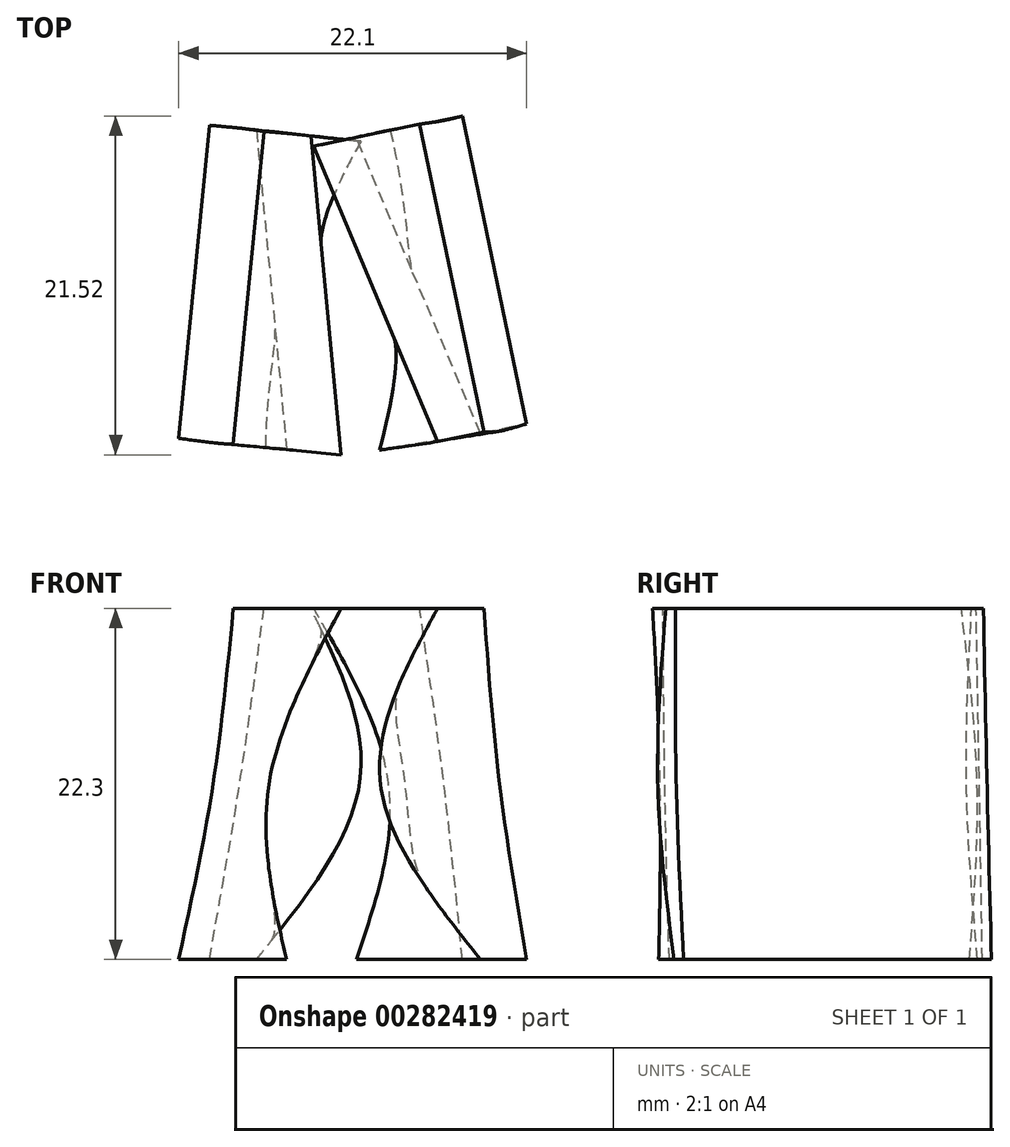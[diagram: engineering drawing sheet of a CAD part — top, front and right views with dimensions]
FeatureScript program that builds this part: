
annotation { "Feature Type Name" : "Feature", "Feature Type Description" : "" }
export const myFeature = defineFeature(function(context is Context, id is Id, definition is map)
    precondition{}
    {
        {
            var Q0;
            Q0=qCreatedBy(makeId("Top.planeOp"),FACE);
            cPlane(context, id + "F0", {"entities" : qUnion([Q0]), "cplaneType" : CPlaneType.OFFSET, "offset" : 11 * mm, "width" : 150 * mm, "height" : 150 * mm});
        }
        {
            var Q0;
            Q0=qCreatedBy(makeId("Top.planeOp"),FACE);
            cPlane(context, id + "F1", {"entities" : qUnion([Q0]), "cplaneType" : CPlaneType.OFFSET, "offset" : 22.3 * mm, "width" : 150 * mm, "height" : 150 * mm});
        }
        {
            var Q0;
            Q0=qCreatedBy(makeId("Top.planeOp"),FACE);
            var sketch = newSketch(context, id + "F2", { "sketchPlane" : qUnion([Q0])});
            skLineSegment(sketch, "E0.bottom", {"start": v(12, -12) * mm, "end": v(-12, -12) * mm, "construction": true});
            skLineSegment(sketch, "E0.top", {"start": v(12, 12) * mm, "end": v(-12, 12) * mm, "construction": true});
            skLineSegment(sketch, "E0.left", {"start": v(12, -12) * mm, "end": v(12, 12) * mm, "construction": true});
            skLineSegment(sketch, "E0.right", {"start": v(-12, -12) * mm, "end": v(-12, 12) * mm, "construction": true});
            skPoint(sketch, "E0.middle", {"position": v(0, 0) * mm});
            skPoint(sketch, "E1.middle", {"position": v(-1.39, -1.74) * mm});
            skLineSegment(sketch, "E2", {"start": v(7.54, 10.91) * mm, "end": v(11.62, -8.64) * mm});
            skLineSegment(sketch, "E3", {"start": v(11.62, -8.64) * mm, "end": v(8.68, -9.26) * mm});
            skLineSegment(sketch, "E4", {"start": v(7.54, 10.91) * mm, "end": v(0.8, 9.5) * mm});
            skLineSegment(sketch, "E5", {"start": v(8.68, -9.26) * mm, "end": v(0.8, 9.5) * mm});
            skPoint(sketch, "E6.middle", {"position": v(3.18, -0.68) * mm});
            skPoint(sketch, "E7.middle", {"position": v(0.21, 0.22) * mm});
            skLineSegment(sketch, "E8", {"start": v(-10.48, -9.56) * mm, "end": v(-8.54, 10.32) * mm});
            skLineSegment(sketch, "E9", {"start": v(-8.54, 10.32) * mm, "end": v(-5.55, 10.03) * mm});
            skLineSegment(sketch, "E10", {"start": v(-10.48, -9.56) * mm, "end": v(-3.64, -10.23) * mm});
            skLineSegment(sketch, "E11", {"start": v(-5.55, 10.03) * mm, "end": v(-3.64, -10.23) * mm});
            skSolve(sketch);
        }
        {
            var Q0;
            Q0=qCreatedBy(id+"F1.planeOp",FACE);
            var sketch = newSketch(context, id + "F3", { "sketchPlane" : qUnion([Q0])});
            skLineSegment(sketch, "E12.bottom", {"start": v(12, -11.91) * mm, "end": v(-12, -11.91) * mm, "construction": true});
            skLineSegment(sketch, "E12.top", {"start": v(12, 12.09) * mm, "end": v(-12, 12.09) * mm, "construction": true});
            skLineSegment(sketch, "E12.left", {"start": v(12, -11.91) * mm, "end": v(12, 12.09) * mm, "construction": true});
            skLineSegment(sketch, "E12.right", {"start": v(-12, -11.91) * mm, "end": v(-12, 12.09) * mm, "construction": true});
            skPoint(sketch, "E12.middle", {"position": v(0, 0.09) * mm});
            skPoint(sketch, "E13.middle", {"position": v(-1.38, -1.65) * mm});
            skLineSegment(sketch, "E14", {"start": v(4.82, 10.4) * mm, "end": v(8.9, -9.16) * mm});
            skLineSegment(sketch, "E15", {"start": v(8.9, -9.16) * mm, "end": v(5.96, -9.77) * mm});
            skLineSegment(sketch, "E16", {"start": v(4.82, 10.4) * mm, "end": v(-1.92, 8.99) * mm});
            skLineSegment(sketch, "E17", {"start": v(5.96, -9.77) * mm, "end": v(-1.92, 8.99) * mm});
            skPoint(sketch, "E18.middle", {"position": v(3.18, -0.6) * mm});
            skPoint(sketch, "E19.middle", {"position": v(0.22, 0.3) * mm});
            skLineSegment(sketch, "E20", {"start": v(-7.02, -9.94) * mm, "end": v(-5.07, 9.94) * mm});
            skLineSegment(sketch, "E21", {"start": v(-5.07, 9.94) * mm, "end": v(-2.09, 9.64) * mm});
            skLineSegment(sketch, "E22", {"start": v(-7.02, -9.94) * mm, "end": v(-0.17, -10.61) * mm});
            skLineSegment(sketch, "E23", {"start": v(-2.09, 9.64) * mm, "end": v(-0.17, -10.61) * mm});
            skSolve(sketch);
        }
        {
            var Q0;
            Q0=qCreatedBy(id+"F0.planeOp",FACE);
            var sketch = newSketch(context, id + "F4", { "sketchPlane" : qUnion([Q0])});
            skLineSegment(sketch, "E24", {"start": v(-6.64, 10.14) * mm, "end": v(0.98, 9.32) * mm});
            skLineSegment(sketch, "E25", {"start": v(-6.64, 10.14) * mm, "end": v(-8.32, -9.84) * mm});
            skLineSegment(sketch, "E26", {"start": v(-8.32, -9.84) * mm, "end": v(-4.77, -10.14) * mm});
            skArc(sketch, "E27", {"start": v(0.98, 9.32) * mm, "mid": v(-3.14, -0.04) * mm, "end": v(-4.77, -10.14) * mm});
            skLineSegment(sketch, "E28", {"start": v(9.92, -9.1) * mm, "end": v(2.35, -10.28) * mm});
            skLineSegment(sketch, "E29", {"start": v(9.92, -9.1) * mm, "end": v(6.38, 10.63) * mm});
            skLineSegment(sketch, "E30", {"start": v(6.38, 10.63) * mm, "end": v(2.87, 10) * mm});
            skArc(sketch, "E31", {"start": v(2.35, -10.28) * mm, "mid": v(3.9, -0.17) * mm, "end": v(2.87, 10) * mm});
            skSolve(sketch);
        }
        {
            var Q0;
            Q0=makeQuery(id+"F2.imprint","IMPRINT",FACE,{"disambiguationData":[TD([[makeQuery(id+"F2.imprint","IMPRINT",EDGE,{"derivedFrom":sQuery(id+"F2.wireOp",EDGE,"E8")}),-1.0]])]});
            var Q1;
            Q1=makeQuery(id+"F4.imprint","IMPRINT",FACE,{"disambiguationData":[TD([[makeQuery(id+"F4.imprint","IMPRINT",EDGE,{"derivedFrom":sQuery(id+"F4.wireOp",EDGE,"E24")}),-1.0]])]});
            var Q2;
            Q2=makeQuery(id+"F3.imprint","IMPRINT",FACE,{"disambiguationData":[TD([[makeQuery(id+"F3.imprint","IMPRINT",EDGE,{"derivedFrom":sQuery(id+"F3.wireOp",EDGE,"E20")}),-1.0]])]});
            loft(context, id + "F5", {"sheetProfilesArray" : [{ "sheetProfileEntities" : qUnion([Q0]) }, { "sheetProfileEntities" : qUnion([Q1]) }, { "sheetProfileEntities" : qUnion([Q2]) }]});
        }
        {
            var Q0;
            Q0=makeQuery(id+"F2.imprint","IMPRINT",FACE,{"disambiguationData":[TD([[makeQuery(id+"F2.imprint","IMPRINT",EDGE,{"derivedFrom":sQuery(id+"F2.wireOp",EDGE,"E2")}),-1.0]])]});
            var Q1;
            Q1=makeQuery(id+"F4.imprint","IMPRINT",FACE,{"disambiguationData":[TD([[makeQuery(id+"F4.imprint","IMPRINT",EDGE,{"derivedFrom":sQuery(id+"F4.wireOp",EDGE,"E28")}),-1.0]])]});
            var Q2;
            Q2=makeQuery(id+"F3.imprint","IMPRINT",FACE,{"disambiguationData":[TD([[makeQuery(id+"F3.imprint","IMPRINT",EDGE,{"derivedFrom":sQuery(id+"F3.wireOp",EDGE,"E14")}),-1.0]])]});
            loft(context, id + "F6", {"sheetProfilesArray" : [{ "sheetProfileEntities" : qUnion([Q0]) }, { "sheetProfileEntities" : qUnion([Q1]) }, { "sheetProfileEntities" : qUnion([Q2]) }]});
        }
    });
